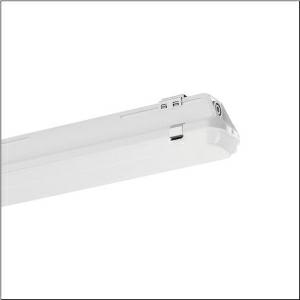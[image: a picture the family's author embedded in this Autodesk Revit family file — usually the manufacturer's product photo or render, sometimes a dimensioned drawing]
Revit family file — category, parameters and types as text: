
# Revit family: monsun_r__21_emergency_51fb10dp437c3h_1bbe
name_source: partatom
category: Lighting Fixtures
units: mm (PartAtom-declared; Revit-internal decimal feet)

## family parameters
Cut with Voids When Loaded = No
Host = Face
Light Source = No
Part Type = Normal
Room Calculation Point = No
Round Connector Dimension = Use Diameter
Shared = No

## types (1)
- --- (1 x LED, 3860 lm, 25.5 W, 4000K)
    Apparent Load = 26 VA
    CIE Flux Codes = 47 77 93 94 100
    Color Rendering = 80
    Color Temperature = 4000K
    Default Elevation = 1800 mm
    Description = Monsun® 21 emergency, damp-proof luminaire, chain hanger, primary optical cover: enclosure, of PMMA, light emission: direct distribution, primary light characteristic: symmetric, installation type: vertical mounting, horizontal mounting, surface-mounted, suspended mounting, LED, rated luminous flux: 3.860lm, luminous efficacy: 178lm/W, light colour: 840, colour temperature: 4000K, control gear: DALI 2, with terminal, 5+3-pole, max. 2.5mm², mains connection: 220..240V, AC, 50/60Hz, rated input power: 26W, control gear: single battery element, battery: LiFePO4, 9Ah, housing, of glass-fibre reinforced polyester, uncoated, bright grey, incl. chain hanger, length: 1.590mm, width: 90mm, height: 88mm, clip for enclosure, of stainless steel (V2A), ceiling mounting element, of stainless steel (V2A), chain hanger, of stainless steel (V2A), protection rating (complete): IP66, insulation class (complete): insulation class I (protective earthing), certification: CE, UKCA, protection symbol: D, impact resistance: IK04, permissible operating ambient temperature: +5..+25°C, standard: EN 50419, EN 60598-2-1, EN 60598-2-22, corresponds to IFS (International Featured Standards) requirements for safety and quality in the food industry, for indoor or canopied outdoor use, no direct snow, no direct sun, no direct rain, LABS conformity tested according to VDMA 24364:2018-05, contact your sales advisor before using the luminaires in applications with unclear chemical exposure, large temperature fluctuations or condensation-forming humidity, packaging unit: 1 piece
    Height = 89 mm
    Lamp = 1 x LED
    Lamp Light Flux = 3860 lm
    Lamp Power = 25.5 W
    Lamp count = 1
    Length = 1590 mm
    Luminous efficacy = 151 lm/W
    Manufacturer = Siteco
    ModVariant = No
    Model = 51FB10DP437C3H
    Mounting Place = Ceiling
    Mounting Type = Surface mounted
    Number of Poles = 1
    OnlyDefault = Yes
    Power Factor = 1
    Product Name = Monsun® 21 emergency
    Product group = damp-proof luminaire
    ProductGroupID = 301
    Protection Class = Protection class I
    Protection Degree = IP 66
    RLX_Detail_Level = 1
    RLX_Emergency_Light_Flux = 0 lm
    RLX_Emergency_Type = 0
    RLX_Emergency_Type_DB = No
    RlxData = <blob elided: 92369 chars, md5=a69a6d8f>
    Socket = socket
    Standby Power = 0 W
    System Light Flux = 3860 lm
    System Power = 26 W
    Type Comments = : luminous flux: 100 % | dim-lin: 254 | 144 mA
    Type Image = l_1319656.jpg
    URL = http://relux.com
    VarID = @adj_051679
    Voltage = 0 V
    Weight = 0.00 kg
    Width = 90 mm

## geometry (parser evidence)
native form markers: Blend x4, Sweep x14
no freeform markers — native parametric forms only
